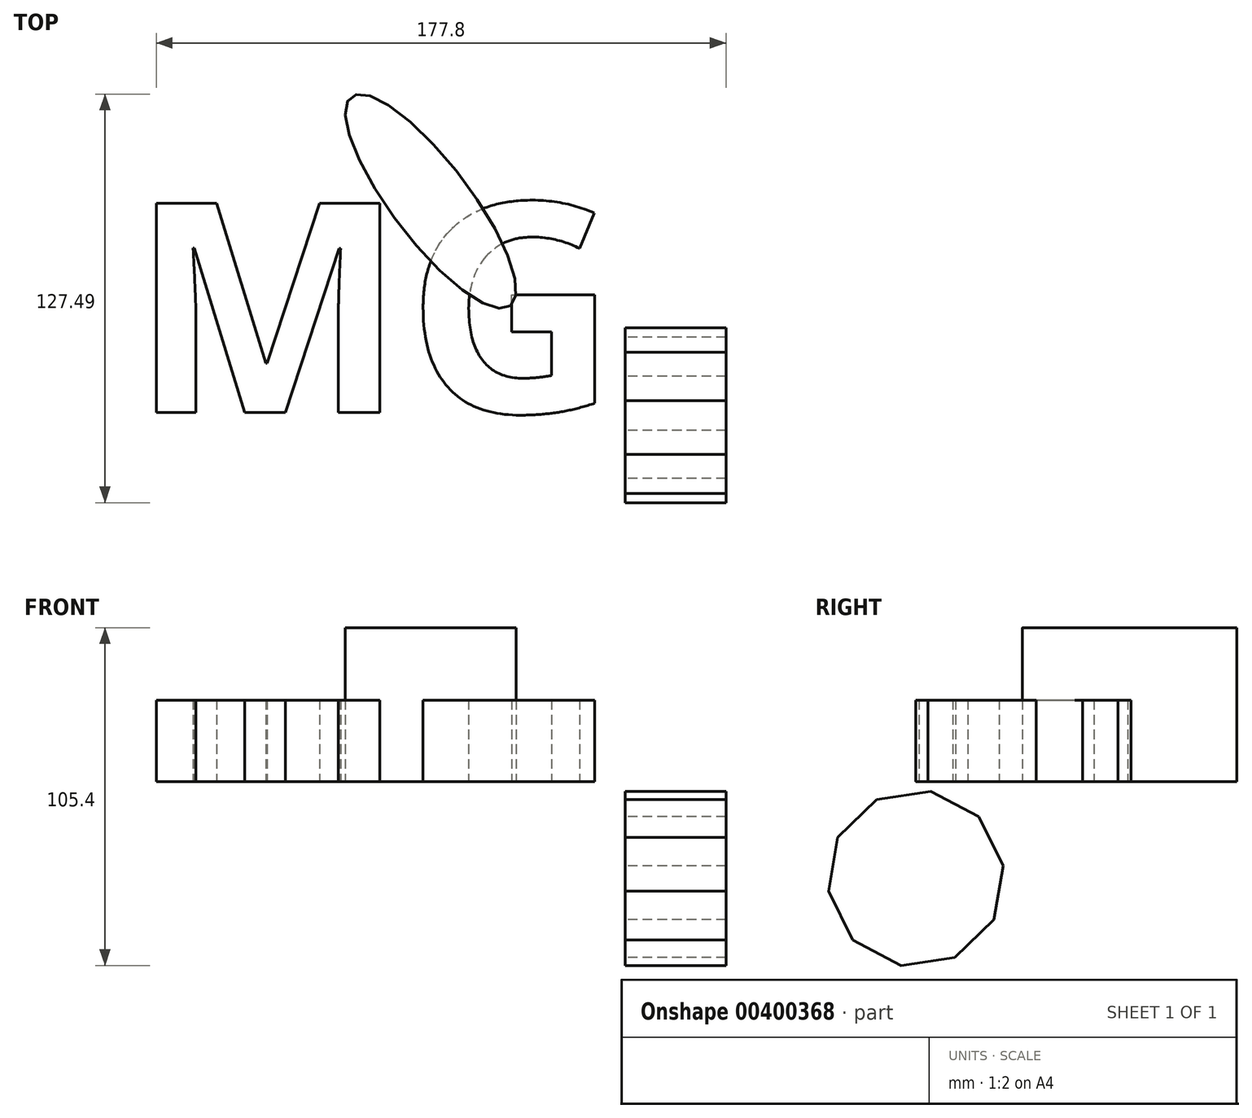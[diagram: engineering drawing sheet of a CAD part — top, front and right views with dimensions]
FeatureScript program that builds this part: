
annotation { "Feature Type Name" : "Feature", "Feature Type Description" : "" }
export const myFeature = defineFeature(function(context is Context, id is Id, definition is map)
    precondition{}
    {
        {
            var Q0;
            Q0=qCreatedBy(makeId("Top.planeOp"),FACE);
            var sketch = newSketch(context, id + "F0", { "sketchPlane" : qUnion([Q0])});
            skEllipse(sketch, "E0", {"center": v(-60.63, 0) * mm, "majorRadius": 41.03 * mm, "minorRadius": 12.16 * mm, "majorAxis": v(0.6, -0.8)});
            skArc(sketch, "E1", {"start": v(-9.55, 36.08) * mm, "mid": v(-23.52, 2.24) * mm, "end": v(13.02, 0) * mm});
            skSolve(sketch);
        }
        {
            var Q0;
            Q0=makeQuery(id+"F0.imprint","IMPRINT",FACE,{"disambiguationData":[TD([[makeQuery(id+"F0.imprint","IMPRINT",EDGE,{"derivedFrom":sQuery(id+"F0.wireOp",EDGE,"E0")}),1.0]])]});
            extrude(context, id + "F1", {"entities" : qUnion([Q0]), "depth" : 48 * mm});
        }
        {
            var Q0;
            Q0=qCreatedBy(makeId("Top.planeOp"),FACE);
            var sketch = newSketch(context, id + "F2", { "sketchPlane" : qUnion([Q0])});
            skText(sketch, "E2", { "text": "MG", "fontName": "OpenSans-Bold.ttf"});
            const initialGuessF2  = {"E2": [-0.15451, -0.06582, 1, 0, 0.06582]};
            skSetInitialGuess(sketch, initialGuessF2);
            skSolve(sketch);
        }
        {
            var Q0;
            Q0 = qSketchRegion(id + "F2", true);
            extrude(context, id + "F3", {"entities" : qUnion([Q0]), "depth" : 25.4 * mm});
        }
        {
            var Q0;
            Q0=qCreatedBy(makeId("Right.planeOp"),FACE);
            var sketch = newSketch(context, id + "F4", { "sketchPlane" : qUnion([Q0])});
            skCircle(sketch, "E3.cCircle", {"center": v(-66.77, -30.25) * mm, "radius": 26.2 * mm, "construction": true});
            skLineSegment(sketch, "E3.0", {"start": v(-62.14, -3.1) * mm, "end": v(-47.07, -11) * mm});
            skLineSegment(sketch, "E3.1", {"start": v(-47.07, -11) * mm, "end": v(-39.52, -26.27) * mm});
            skLineSegment(sketch, "E3.2", {"start": v(-39.52, -26.27) * mm, "end": v(-42.39, -43.04) * mm});
            skLineSegment(sketch, "E3.3", {"start": v(-42.39, -43.04) * mm, "end": v(-54.56, -54.93) * mm});
            skLineSegment(sketch, "E3.4", {"start": v(-54.56, -54.93) * mm, "end": v(-71.4, -57.4) * mm});
            skLineSegment(sketch, "E3.5", {"start": v(-71.4, -57.4) * mm, "end": v(-86.47, -49.49) * mm});
            skLineSegment(sketch, "E3.6", {"start": v(-86.47, -49.49) * mm, "end": v(-94.02, -34.23) * mm});
            skLineSegment(sketch, "E3.7", {"start": v(-94.02, -34.23) * mm, "end": v(-91.16, -17.45) * mm});
            skLineSegment(sketch, "E3.8", {"start": v(-91.16, -17.45) * mm, "end": v(-78.98, -5.56) * mm});
            skLineSegment(sketch, "E3.9", {"start": v(-78.98, -5.56) * mm, "end": v(-62.14, -3.1) * mm});
            skPoint(sketch, "E3.0.midPoint", {"position": v(-54.6, -7.06) * mm});
            skSolve(sketch);
        }
        {
            var Q0;
            Q0=makeQuery(id+"F4.imprint","IMPRINT",FACE,{"disambiguationData":[TD([[makeQuery(id+"F4.imprint","IMPRINT",EDGE,{"derivedFrom":sQuery(id+"F4.wireOp",EDGE,"E3.0")}),-1.0]])]});
            extrude(context, id + "F5", {"entities" : qUnion([Q0]), "depth" : 31.5 * mm});
        }
    });
